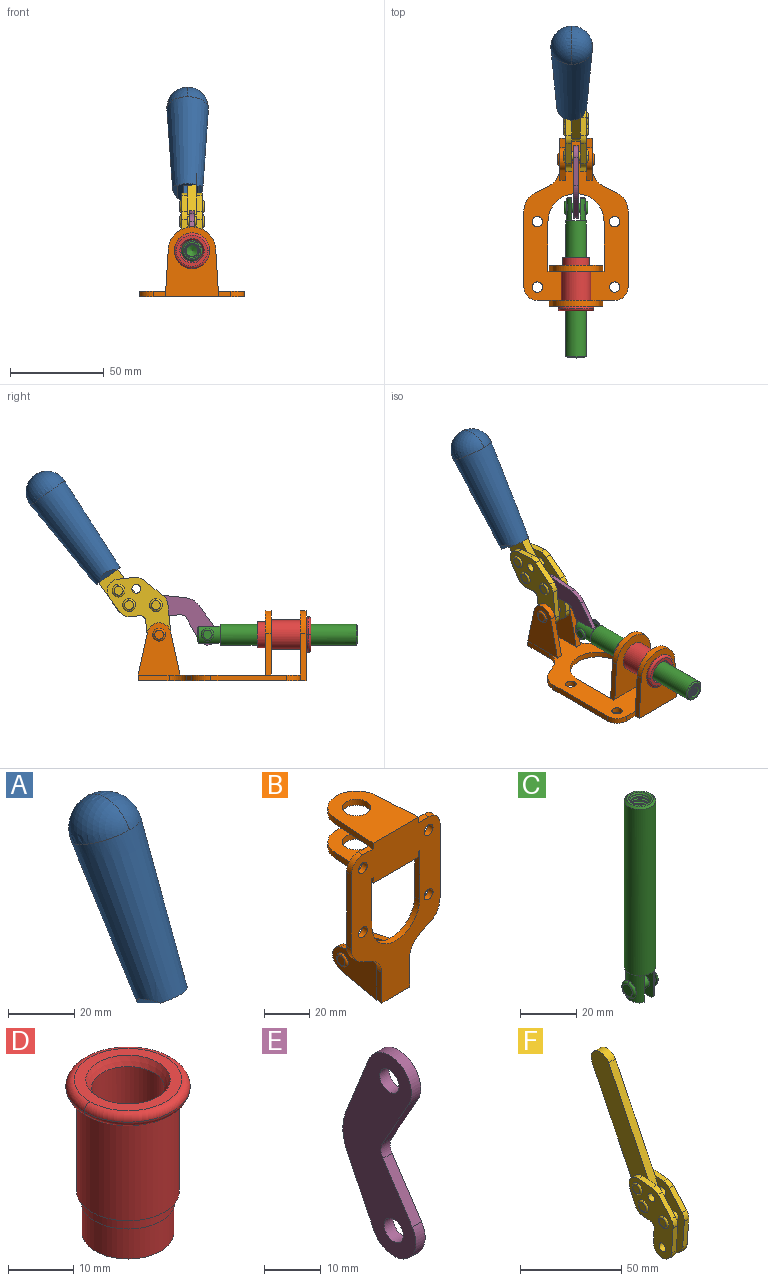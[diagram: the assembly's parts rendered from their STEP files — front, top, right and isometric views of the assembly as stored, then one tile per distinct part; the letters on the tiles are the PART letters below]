
ASSEMBLY  parts=6 mates=6
PART A: 11 faces, bbox 22.3x42.6x64.5 mm
  f0: sphere r=11.13mm, area 411.4mm2, adj f1,f8
  f1: cone r=11.11mm half-angle=3.3deg, axis (0,0.44,0.9), area 3251.8mm2, adj f0,f7,f8,f9,f10
  f2: cylinder r=6.16mm len=11.7mm, axis (1,0,0), area 89.5mm2, adj f3,f4,f5,f6
  f3: plane 60.23x36.75mm, normal (-1,0,0), area 763.6mm2, adj f2,f4,f6,f10
  f4: plane 51.37x25.05mm, normal (0,0.9,-0.44), area 264.2mm2, adj f2,f3,f5,f10
  f5: plane 60.23x36.75mm, normal (1,0,0), area 763.6mm2, adj f2,f4,f6,f10
  f6: plane 51.37x25.05mm, normal (0,-0.9,0.44), area 264.2mm2, adj f2,f3,f5,f10
  f7: plane 9.95x5.95mm, normal (0.71,-0.31,-0.64), area 25.8mm2, adj f1,f10
  f8: sphere r=11.13mm, area 411.4mm2, adj f0,f1
  f9: plane 9.95x5.95mm, normal (-0.71,-0.31,-0.64), area 25.8mm2, adj f1,f10
  f10: plane 14.27x11.38mm, normal (0,-0.44,-0.9), area 106.7mm2, adj f1,f3,f4,f5,f6,f7,f9
PART B: 55 faces, bbox 55.7x37.4x89.8 mm
  f0: torus R=2.41mm, axis (-1,0,0), area 15mm2, adj f11,f15,f25
  f1: torus R=2.41mm, axis (-1,0,0), area 15mm2, adj f10,f12,f22
  f2: cylinder r=2.78mm len=5.56mm, axis (0,-1,0), area 54.2mm2, adj f30,f54
  f3: cylinder r=14.99mm len=29.97mm, axis (0,-1,0), area 145.9mm2, adj f30,f49,f53,f54
  f4: cylinder r=2.78mm len=5.56mm, axis (0,-1,0), area 54.2mm2, adj f30,f54
  f5: cylinder r=2.78mm len=5.56mm, axis (0,-1,0), area 54.2mm2, adj f30,f54
  f6: cylinder r=2.78mm len=5.56mm, axis (0,-1,0), area 54.2mm2, adj f30,f54
  f7: cylinder r=6.35mm len=12.7mm, axis (0,0,1), area 123.6mm2, adj f27,f51
  f8: cylinder r=6.35mm len=12.7mm, axis (0,0,-1), area 124.7mm2, adj f21,f35
  f9: cylinder r=2.41mm len=11.18mm, axis (-1,0,0), area 169.4mm2, adj f16,f19
  f10: plane 4.83x4.83mm, normal (1,0,0), area 18.3mm2, adj f1,f12
  f11: plane 4.83x4.83mm, normal (-1,0,0), area 18.3mm2, adj f0,f15
  f12: torus R=2.41mm, axis (-1,0,0), area 15mm2, adj f1,f10,f22
  f13: cylinder r=6.35mm len=12.41mm, axis (1,0,0), area 53.4mm2, adj f18,f19,f22,f23
  f14: cylinder r=6.35mm len=12.41mm, axis (-1,0,0), area 53.4mm2, adj f16,f17,f24,f25
  f15: torus R=2.41mm, axis (-1,0,0), area 15mm2, adj f0,f11,f25
  f16: plane 27.86x22.35mm, normal (1,0,0), area 425.4mm2, adj f9,f14,f17,f24,f30
  f17: plane 22.86x4.97mm, normal (0,0.21,0.98), area 72.5mm2, adj f14,f16,f25,f30
  f18: plane 22.86x4.97mm, normal (0,0.21,0.98), area 72.5mm2, adj f13,f19,f22,f30
  f19: plane 27.86x22.35mm, normal (-1,0,0), area 425.4mm2, adj f9,f13,f18,f23,f30
  f20: cylinder r=12.7mm len=25.35mm, axis (0,0,-1), area 119.8mm2, adj f21,f34,f35,f36
  f21: plane 34.21x28.07mm, normal (0,0,-1), area 702.4mm2, adj f8,f20,f30,f34,f36
  f22: plane 27.96x22.45mm, normal (1,0,0), area 407.2mm2, adj f1,f12,f13,f18,f23,f30,f42,f43
  f23: plane 22.86x4.97mm, normal (0,0.21,-0.98), area 72.5mm2, adj f13,f19,f22,f44
  f24: plane 22.86x4.97mm, normal (0,0.21,-0.98), area 72.5mm2, adj f14,f16,f25,f44
  f25: plane 27.86x22.35mm, normal (-1,0,0), area 407.1mm2, adj f0,f14,f15,f17,f24,f30,f45,f46
  f26: plane 3.1x0.95mm, normal (0,0,-1), area 2.7mm2, adj f30,f49,f50,f54
  f27: plane 34.21x28.07mm, normal (0,0,1), area 702.4mm2, adj f7,f28,f30,f50,f52
  f28: cylinder r=12.7mm len=25.35mm, axis (0,0,1), area 118.8mm2, adj f27,f50,f51,f52
  f29: plane 3.1x0.95mm, normal (0,0,-1), area 2.7mm2, adj f30,f52,f53,f54
  f30: plane 86.54x55.63mm, normal (0,1,0), area 2362.9mm2, adj f2,f3,f4,f5,f6,f16,f17,f18
  f31: plane 40.56x3.1mm, normal (-1,0,0), area 125.7mm2, adj f30,f32,f48,f54
  f32: cylinder r=7.11mm len=7.11mm, axis (0,-1,0), area 34.6mm2, adj f30,f31,f33,f54
  f33: plane 6.67x3.1mm, normal (0,0,1), area 20.4mm2, adj f30,f32,f34,f54
  f34: plane 25.39x3.13mm, normal (-1,0.06,0), area 79.5mm2, adj f20,f21,f33,f35,f54
  f35: plane 37.31x28.45mm, normal (0,0,1), area 789.9mm2, adj f8,f20,f34,f36,f54
  f36: plane 25.39x3.13mm, normal (1,0.06,0), area 79.5mm2, adj f20,f21,f35,f37,f54
  f37: plane 6.67x3.1mm, normal (0,0,1), area 20.4mm2, adj f30,f36,f38,f54
  f38: cylinder r=7.11mm len=7.11mm, axis (0,-1,0), area 34.6mm2, adj f30,f37,f39,f54
  f39: plane 40.56x3.1mm, normal (1,0,0), area 125.7mm2, adj f30,f38,f40,f54
  f40: cylinder r=11.18mm len=10.16mm, axis (0,-1,0), area 39.5mm2, adj f30,f39,f41,f54
  f41: plane 6.09x3.1mm, normal (0.42,0,-0.91), area 20.8mm2, adj f30,f40,f42,f54
  f42: cylinder r=11.18mm len=9.41mm, axis (0,-1,0), area 37.2mm2, adj f22,f30,f41,f43,f54
  f43: plane 16.5x3.1mm, normal (1,0,0), area 51.1mm2, adj f22,f42,f44,f54
  f44: plane 17.37x3.1mm, normal (0,0,-1), area 53.8mm2, adj f23,f24,f30,f43,f45,f54
  f45: plane 16.5x3.1mm, normal (-1,0,0), area 51.1mm2, adj f25,f44,f46,f54
  f46: cylinder r=11.18mm len=9.41mm, axis (0,-1,0), area 37.2mm2, adj f25,f30,f45,f47,f54
  f47: plane 6.09x3.1mm, normal (-0.42,0,-0.91), area 20.8mm2, adj f30,f46,f48,f54
  f48: cylinder r=11.18mm len=10.16mm, axis (0,-1,0), area 39.5mm2, adj f30,f31,f47,f54
  f49: plane 26.54x3.1mm, normal (-1,0,0), area 82.3mm2, adj f3,f26,f30,f54
  f50: plane 25.39x3.1mm, normal (1,0.06,0), area 78.8mm2, adj f26,f27,f28,f51,f54
  f51: plane 37.31x28.45mm, normal (0,0,-1), area 789.9mm2, adj f7,f28,f50,f52,f54
  f52: plane 25.39x3.1mm, normal (-1,0.06,0), area 78.8mm2, adj f27,f28,f29,f51,f54
  f53: plane 26.54x3.1mm, normal (1,0,0), area 82.3mm2, adj f3,f29,f30,f54
  f54: plane 89.66x55.63mm, normal (0,-1,0), area 2678.5mm2, adj f2,f3,f4,f5,f6,f26,f29,f31
PART C: 48 faces, bbox 12.6x11.1x86.1 mm
  f0: torus R=2.41mm, axis (-1,0,0), area 15mm2, adj f30,f32,f34
  f1: torus R=2.41mm, axis (-1,0,0), area 15mm2, adj f29,f31,f33
  f2: cylinder r=5.54mm len=72.39mm, axis (0,0,1), area 2518.5mm2, adj f3,f4,f42,f43
  f3: cone r=5.54mm half-angle=45deg, axis (0,0,1), area 7.6mm2, adj f2,f5,f41
  f4: cone r=5.54mm half-angle=45deg, axis (0,0,-1), area 34.9mm2, adj f2,f39
  f5: cylinder r=5.08mm len=11.48mm, axis (0,0,1), area 108.3mm2, adj f3,f7,f8,f41
  f6: cylinder r=2.41mm len=4.83mm, axis (-1,0,0), area 71.2mm2, adj f40,f41
  f7: cylinder r=2.41mm len=4.83mm, axis (-1,0,0), area 7.6mm2, adj f5,f34
  f8: cone r=5.08mm half-angle=45deg, axis (0,0,1), area 10.6mm2, adj f5,f37,f41
  f9: cone r=3.98mm half-angle=45deg, axis (0,0,1), area 17.6mm2, adj f27,f39,f45,f46,f47
  f10: cylinder r=2.41mm len=4.83mm, axis (-1,0,0), area 7.6mm2, adj f33,f38
  f11: cylinder r=3.2mm len=6.4mm, axis (0,0,1), area 78.4mm2, adj f12,f28,f44,f45,f47
  f12: cylinder r=3.2mm len=6.4mm, axis (0,0,1), area 10.5mm2, adj f11,f13,f45,f47
  f13: cylinder r=3.2mm len=6.4mm, axis (0,0,1), area 10.5mm2, adj f12,f14,f45,f47
  f14: cylinder r=3.2mm len=6.4mm, axis (0,0,1), area 10.5mm2, adj f13,f15,f45,f47
  f15: cylinder r=3.2mm len=6.4mm, axis (0,0,1), area 10.5mm2, adj f14,f16,f45,f47
  f16: cylinder r=3.2mm len=6.4mm, axis (0,0,1), area 10.5mm2, adj f15,f17,f45,f47
  f17: cylinder r=3.2mm len=6.4mm, axis (0,0,1), area 10.5mm2, adj f16,f18,f45,f47
  f18: cylinder r=3.2mm len=6.4mm, axis (0,0,1), area 10.5mm2, adj f17,f19,f45,f47
  f19: cylinder r=3.2mm len=6.4mm, axis (0,0,1), area 10.5mm2, adj f18,f20,f45,f47
  f20: cylinder r=3.2mm len=6.4mm, axis (0,0,1), area 10.5mm2, adj f19,f21,f45,f47
  f21: cylinder r=3.2mm len=6.4mm, axis (0,0,1), area 10.5mm2, adj f20,f22,f45,f47
  f22: cylinder r=3.2mm len=6.4mm, axis (0,0,1), area 10.5mm2, adj f21,f23,f45,f47
  f23: cylinder r=3.2mm len=6.4mm, axis (0,0,1), area 10.5mm2, adj f22,f24,f45,f47
  f24: cylinder r=3.2mm len=6.4mm, axis (0,0,1), area 10.5mm2, adj f23,f25,f45,f47
  f25: cylinder r=3.2mm len=6.4mm, axis (0,0,1), area 10.5mm2, adj f24,f26,f45,f47
  f26: cylinder r=3.2mm len=6.4mm, axis (0,0,1), area 10.5mm2, adj f25,f27,f45,f47
  f27: cylinder r=3.2mm len=6.4mm, axis (0,0,1), area 7.4mm2, adj f9,f26,f45,f47
  f28: cone r=3.2mm half-angle=60deg, axis (0,0,1), area 37.2mm2, adj f11
  f29: plane 4.83x4.83mm, normal (-1,0,0), area 18.3mm2, adj f1,f31
  f30: plane 4.83x4.83mm, normal (1,0,0), area 18.3mm2, adj f0,f32
  f31: torus R=2.41mm, axis (-1,0,0), area 15mm2, adj f1,f29,f33
  f32: torus R=2.41mm, axis (-1,0,0), area 15mm2, adj f0,f30,f34
  f33: plane 6.83x6.83mm, normal (1,0,0), area 18.3mm2, adj f1,f10,f31
  f34: plane 6.83x6.83mm, normal (-1,0,0), area 18.3mm2, adj f0,f7,f32
  f35: cone r=5.08mm half-angle=45deg, axis (0,0,1), area 10.6mm2, adj f36,f38,f40
  f36: plane 7.25x1.97mm, normal (0,0,-1), area 10mm2, adj f35,f40
  f37: plane 7.25x1.97mm, normal (0,0,-1), area 10mm2, adj f8,f41
  f38: cylinder r=5.08mm len=11.48mm, axis (0,0,1), area 108.3mm2, adj f10,f35,f40,f42
  f39: plane 9.55x9.55mm, normal (0,0,1), area 22mm2, adj f4,f9
  f40: plane 12.76x10.09mm, normal (1,0,0), area 95.7mm2, adj f6,f35,f36,f38,f42,f43
  f41: plane 12.76x10.09mm, normal (-1,0,0), area 95.7mm2, adj f3,f5,f6,f8,f37,f43
  f42: cone r=5.54mm half-angle=45deg, axis (0,0,1), area 7.6mm2, adj f2,f38,f40
  f43: plane 11.07x4.7mm, normal (0,0,-1), area 50.4mm2, adj f2,f40,f41
  f44: plane 0.89x0.62mm, normal (-1,0,0), area 0.3mm2, adj f11,f45,f46,f47
  f45: bspline ~24.8x7.63mm, area 266.6mm2, adj f9,f11,f12,f13,f14,f15,f16,f17
  f46: bspline ~24.87x7.63mm, area 73.6mm2, adj f9,f44,f45,f47
  f47: bspline ~24.98x7.63mm, area 272.5mm2, adj f9,f11,f12,f13,f14,f15,f16,f17
PART D: 15 faces, bbox 20.6x20.6x28.7 mm
  f0: torus R=8.26mm, axis (0,0,1), area 56.8mm2, adj f1,f10,f12
  f1: torus R=8.26mm, axis (0,0,1), area 56.8mm2, adj f0,f6,f13
  f2: cylinder r=5.59mm len=25.91mm, axis (0,0,1), area 909.6mm2, adj f3,f4
  f3: cone r=6.86mm half-angle=45deg, axis (0,0,-1), area 70.2mm2, adj f2,f14
  f4: cone r=6.47mm half-angle=30deg, axis (0,0,1), area 66.7mm2, adj f2,f13
  f5: cylinder r=7.04mm len=14.07mm, axis (0,0,1), area 252.6mm2, adj f11,f14
  f6: torus R=8.26mm, axis (0,0,1), area 56.8mm2, adj f1,f12,f13
  f7: cylinder r=7.16mm len=14.33mm, axis (0,0,1), area 91.5mm2, adj f9,f11
  f8: cylinder r=7.86mm len=18.42mm, axis (0,0,1), area 909.6mm2, adj f9,f10
  f9: plane 15.72x15.72mm, normal (0,0,-1), area 33mm2, adj f7,f8
  f10: plane 16.51x16.51mm, normal (0,0,-1), area 19.9mm2, adj f0,f8,f12
  f11: plane 14.33x14.33mm, normal (0,0,-1), area 5.7mm2, adj f5,f7
  f12: torus R=8.26mm, axis (0,0,1), area 56.8mm2, adj f0,f6,f10
  f13: plane 16.51x16.51mm, normal (0,0,1), area 82.7mm2, adj f1,f4,f6
  f14: plane 14.07x14.07mm, normal (0,0,-1), area 7.8mm2, adj f3,f5
PART E: 12 faces, bbox 2.3x18.2x42.8 mm
  f0: cylinder r=2.4mm len=4.8mm, axis (1,0,0), area 34.9mm2, adj f4,f11
  f1: cylinder r=10.41mm len=8.47mm, axis (1,0,0), area 20.2mm2, adj f4,f9,f10,f11
  f2: cylinder r=3.05mm len=3.16mm, axis (1,0,0), area 7.7mm2, adj f4,f6,f7,f11
  f3: cylinder r=2.4mm len=4.8mm, axis (1,0,0), area 34.9mm2, adj f4,f11
  f4: plane 42.81x18.23mm, normal (-1,0,0), area 414.1mm2, adj f0,f1,f2,f3,f5,f6,f7,f8
  f5: cylinder r=5.54mm len=10.67mm, axis (1,0,0), area 41.8mm2, adj f4,f6,f10,f11
  f6: plane 11.66x6.53mm, normal (0,-0.87,-0.49), area 30.9mm2, adj f2,f4,f5,f11
  f7: plane 11.17x7.33mm, normal (0,-0.84,0.55), area 30.9mm2, adj f2,f4,f8,f11
  f8: cylinder r=5.54mm len=10.51mm, axis (1,0,0), area 41.8mm2, adj f4,f7,f9,f11
  f9: plane 13.67x6.67mm, normal (0,0.9,-0.44), area 35.1mm2, adj f1,f4,f8,f11
  f10: plane 14.1x5.7mm, normal (0,0.93,0.37), area 35.1mm2, adj f1,f4,f5,f11
  f11: plane 42.81x18.23mm, normal (1,0,0), area 414.1mm2, adj f0,f1,f2,f3,f5,f6,f7,f8
PART F: 59 faces, bbox 12.9x60.2x99.6 mm
  f0: torus R=2.39mm, axis (-1,0,0), area 14.9mm2, adj f20,f43,f51
  f1: torus R=2.39mm, axis (-1,0,0), area 14.9mm2, adj f19,f42,f51
  f2: torus R=2.39mm, axis (-1,0,0), area 14.9mm2, adj f18,f35,f51
  f3: torus R=2.39mm, axis (-1,0,0), area 14.9mm2, adj f14,f17,f23
  f4: torus R=2.39mm, axis (-1,0,0), area 14.9mm2, adj f13,f16,f23
  f5: torus R=2.39mm, axis (-1,0,0), area 14.9mm2, adj f12,f15,f23
  f6: cylinder r=2.39mm len=4.78mm, axis (1,0,0), area 46.5mm2, adj f48,f50,f51
  f7: cylinder r=2.39mm len=4.78mm, axis (1,0,0), area 46.5mm2, adj f50,f51
  f8: cylinder r=6.35mm len=12.68mm, axis (1,0,0), area 61.8mm2, adj f38,f39,f50,f51
  f9: cylinder r=2.39mm len=4.78mm, axis (-1,0,0), area 70.5mm2, adj f46,f50
  f10: cylinder r=2.39mm len=4.78mm, axis (-1,0,0), area 46.5mm2, adj f23,f45,f46
  f11: cylinder r=2.39mm len=4.78mm, axis (-1,0,0), area 46.5mm2, adj f23,f46
  f12: plane 4.78x4.78mm, normal (1,0,0), area 17.9mm2, adj f5,f15
  f13: plane 4.78x4.78mm, normal (1,0,0), area 17.9mm2, adj f4,f16
  f14: plane 4.78x4.78mm, normal (1,0,0), area 17.9mm2, adj f3,f17
  f15: torus R=2.39mm, axis (-1,0,0), area 14.9mm2, adj f5,f12,f23
  f16: torus R=2.39mm, axis (-1,0,0), area 14.9mm2, adj f4,f13,f23
  f17: torus R=2.39mm, axis (-1,0,0), area 14.9mm2, adj f3,f14,f23
  f18: plane 4.78x4.78mm, normal (-1,0,0), area 17.9mm2, adj f2,f35
  f19: plane 4.78x4.78mm, normal (-1,0,0), area 17.9mm2, adj f1,f42
  f20: plane 4.78x4.78mm, normal (-1,0,0), area 17.9mm2, adj f0,f43
  f21: plane 2.26x0.2mm, normal (1,0,0), area 0.2mm2, adj f31,f44
  f22: plane 2.26x0.2mm, normal (-1,0,0), area 0.2mm2, adj f41,f44
  f23: plane 39.37x30.77mm, normal (1,0,0), area 565.5mm2, adj f3,f4,f5,f10,f11,f15,f16,f17
  f24: cylinder r=6.1mm len=4.15mm, axis (-1,0,0), area 14.7mm2, adj f23,f25,f32,f46
  f25: plane 10.25x9.01mm, normal (0,-0.75,0.66), area 42.3mm2, adj f23,f24,f26,f46
  f26: cylinder r=6.35mm len=4.64mm, axis (-1,0,0), area 15.6mm2, adj f23,f25,f27,f46
  f27: plane 15.84x3.1mm, normal (0,-1,-0.07), area 49.2mm2, adj f23,f26,f28,f46
  f28: cylinder r=6.35mm len=12.68mm, axis (-1,0,0), area 61.8mm2, adj f23,f27,f29,f46
  f29: plane 8.11x3.1mm, normal (0,1,0.07), area 25.2mm2, adj f23,f28,f30,f46
  f30: cylinder r=3.05mm len=3.25mm, axis (-1,0,0), area 14.8mm2, adj f23,f29,f31,f46
  f31: plane 5.99x3.1mm, normal (0,0.07,-1), area 18.6mm2, adj f21,f23,f30,f44,f46
  f32: plane 9.5x3.1mm, normal (0,-0.07,1), area 29.5mm2, adj f23,f24,f33,f46,f47
  f33: cylinder r=6.1mm len=8.63mm, axis (-1,0,0), area 39.1mm2, adj f23,f32,f34,f47
  f34: plane 8.65x3.96mm, normal (0,0.91,-0.42), area 29.5mm2, adj f23,f33,f44,f47
  f35: torus R=2.39mm, axis (-1,0,0), area 14.9mm2, adj f2,f18,f51
  f36: plane 10.25x9.01mm, normal (0,-0.75,0.66), area 42.3mm2, adj f37,f49,f50,f51
  f37: cylinder r=6.35mm len=4.64mm, axis (1,0,0), area 15.6mm2, adj f36,f38,f50,f51
  f38: plane 15.84x3.1mm, normal (0,-1,-0.07), area 49.2mm2, adj f8,f37,f50,f51
  f39: plane 8.11x3.1mm, normal (0,1,0.07), area 25.2mm2, adj f8,f40,f50,f51
  f40: cylinder r=3.05mm len=3.25mm, axis (1,0,0), area 14.8mm2, adj f39,f41,f50,f51
  f41: plane 5.99x3.1mm, normal (0,0.07,-1), area 18.6mm2, adj f22,f40,f44,f50,f51
  f42: torus R=2.39mm, axis (-1,0,0), area 14.9mm2, adj f1,f19,f51
  f43: torus R=2.39mm, axis (-1,0,0), area 14.9mm2, adj f0,f20,f51
  f44: cylinder r=6.35mm len=12.12mm, axis (-1,0,0), area 128.9mm2, adj f21,f22,f23,f31,f34,f41,f46,f47
  f45: plane 2.65x1.35mm, normal (1,0,0), area 1mm2, adj f10,f55
  f46: plane 39.08x20.42mm, normal (-1,0,0), area 412.5mm2, adj f9,f10,f11,f24,f25,f26,f27,f28
  f47: plane 77.62x39.82mm, normal (1,0,0), area 850mm2, adj f32,f33,f34,f44,f53,f54,f55
  f48: plane 2.65x1.35mm, normal (-1,0,0), area 1mm2, adj f6,f55
  f49: cylinder r=6.1mm len=4.15mm, axis (1,0,0), area 14.7mm2, adj f36,f50,f51,f56
  f50: plane 39.08x20.42mm, normal (1,0,0), area 412.5mm2, adj f6,f7,f8,f9,f36,f37,f38,f39
  f51: plane 39.37x30.77mm, normal (-1,0,0), area 565.5mm2, adj f0,f1,f2,f6,f7,f8,f35,f36
  f52: plane 8.65x3.96mm, normal (0,0.91,-0.42), area 29.5mm2, adj f44,f51,f57,f58
  f53: plane 68.49x33.4mm, normal (0,0.9,-0.44), area 358.1mm2, adj f44,f47,f54,f58
  f54: cylinder r=6.35mm len=12.06mm, axis (1,0,0), area 93.7mm2, adj f47,f53,f55,f58
  f55: plane 68.49x33.4mm, normal (0,-0.9,0.44), area 358.1mm2, adj f44,f45,f46,f47,f48,f50,f54,f58
  f56: plane 9.5x3.1mm, normal (0,-0.07,1), area 29.5mm2, adj f49,f50,f51,f57,f58
  f57: cylinder r=6.1mm len=8.63mm, axis (1,0,0), area 39.1mm2, adj f51,f52,f56,f58
  f58: plane 77.62x39.82mm, normal (-1,0,0), area 850mm2, adj f44,f52,f53,f54,f55,f56,f57
PLACE A rot(axis=(-1,0,0),10deg) t=(-2.31,14.66,60.49)mm
PLACE B rot(axis=(1,0,0),90deg) t=(0,1.23,0)mm fixed
PLACE C rot(axis=(1,0,0),90deg) t=(0,22.91,0)mm
PLACE D rot(axis=(1,0,0),90deg) t=(0,1.23,0)mm
PLACE E rot(axis=(1,0,0),121.8deg) t=(0,33.56,11.86)mm
PLACE F rot(axis=(-1,0,0),10deg) t=(0,14.66,60.49)mm
MATE fastened F.f54 <-> A.f2  axis (1,0,0) through (0,94.13,102.1)mm
MATE revolute B.f0 <-> F.f7  axis (-1,0,0) through (0,33.32,24.61)mm
MATE fastened D.f2 <-> B.f7  axis (0,-1,0) through (0,-45.16,24.61)mm
MATE revolute E.f3 <-> F.f4  axis (1,0,0) through (0,34.98,40.4)mm
MATE revolute C.f6 <-> E.f5  axis (-1,0,0) through (0,7.44,24.61)mm
MATE slider C.f2 <-> D.f2  axis (0,-1,0) through (0,-35.87,24.61)mm
